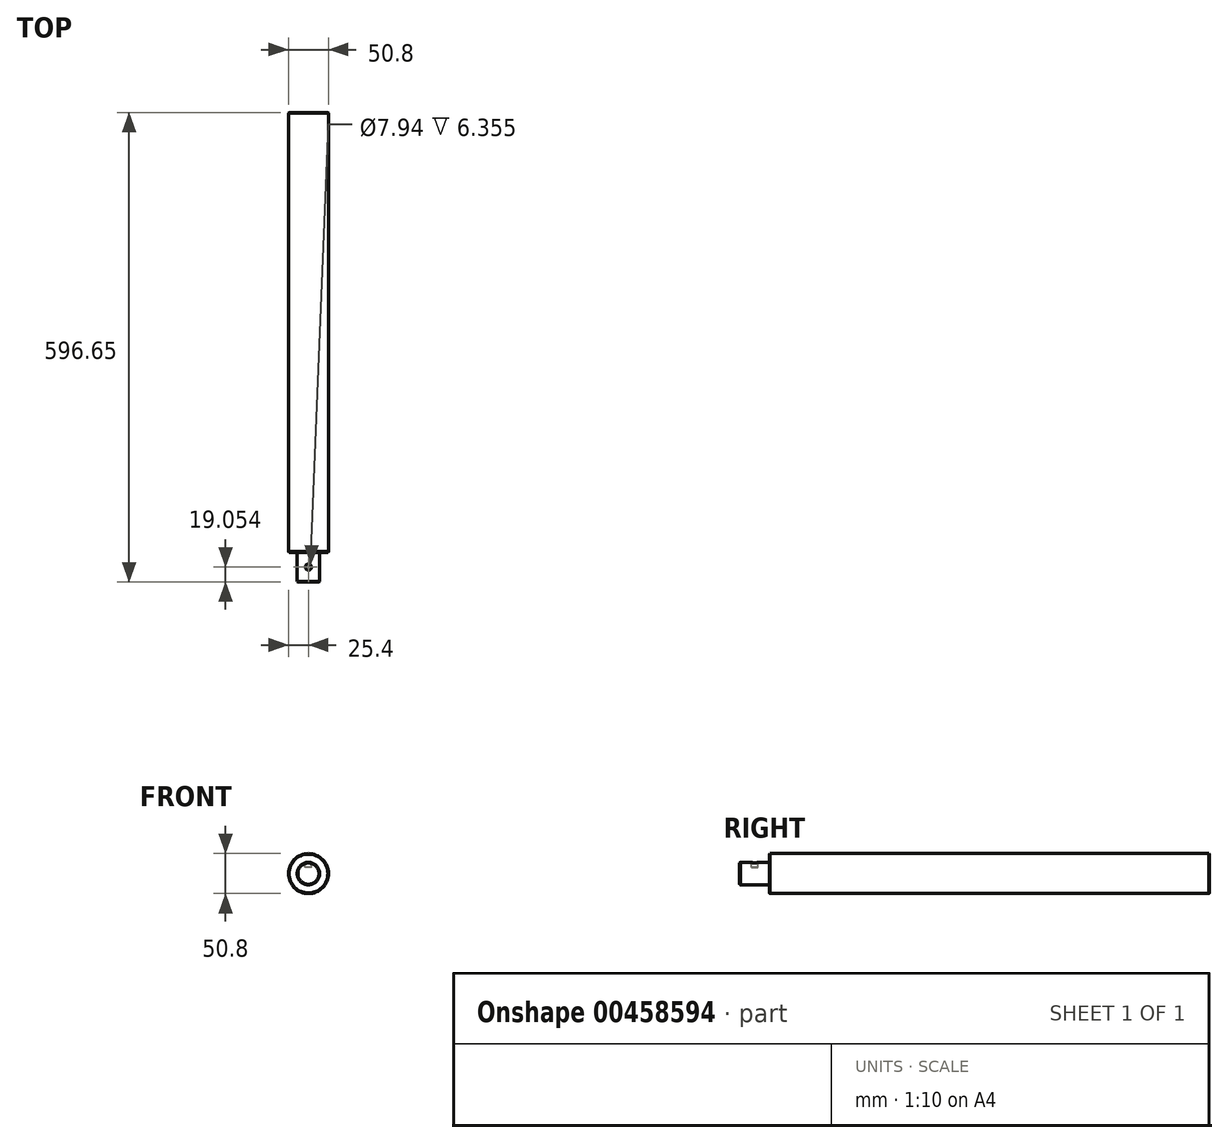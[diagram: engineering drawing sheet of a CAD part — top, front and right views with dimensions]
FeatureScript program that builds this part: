
annotation { "Feature Type Name" : "Feature", "Feature Type Description" : "" }
export const myFeature = defineFeature(function(context is Context, id is Id, definition is map)
    precondition{}
    {
        {
            var Q0;
            Q0=qCreatedBy(makeId("Front.planeOp"),FACE);
            var sketch = newSketch(context, id + "F0", { "sketchPlane" : qUnion([Q0])});
            skCircle(sketch, "E0", {"center": v(0, 0) * mm, "radius": 25.4 * mm});
            skSolve(sketch);
        }
        {
            var Q0;
            Q0 = qSketchRegion(id + "F0", true);
            extrude(context, id + "F1", {"entities" : qUnion([Q0]), "depth" : 558.8 * mm});
        }
        {
            var Q0;
            Q0=makeQuery(id+"F1.opExtrude","CAP_FACE",FACE,{"disambiguationData":[OSD([sQuery(id+"F0.wireOp",EDGE,"E0")])],"isStart":false});
            var sketch = newSketch(context, id + "F2", { "sketchPlane" : qUnion([Q0])});
            skCircle(sketch, "E1", {"center": v(0, 0) * mm, "radius": 14.22 * mm});
            skSolve(sketch);
        }
        {
            var Q0;
            Q0 = qSketchRegion(id + "F2", true);
            extrude(context, id + "F3", {"entities" : qUnion([Q0]), "operationType" : NewBodyOperationType.ADD, "depth" : 37.85 * mm});
        }
        {
            var Q0;
            Q0=makeQuery(id+"F3.opExtrude","CAP_EDGE",EDGE,{"disambiguationData":[OSD([sQuery(id+"F2.wireOp",EDGE,"E1")])],"isStart":false});
            var Q1;
            Q1=makeQuery(id+"F1.opExtrude","CAP_EDGE",EDGE,{"disambiguationData":[OSD([sQuery(id+"F0.wireOp",EDGE,"E0")])],"isStart":false});
            var Q2;
            Q2=makeQuery(id+"F1.opExtrude","CAP_EDGE",EDGE,{"disambiguationData":[OSD([sQuery(id+"F0.wireOp",EDGE,"E0")])],"isStart":true});
            chamfer(context, id + "F4", {"entities" : qUnion([Q0, Q1, Q2]), "width" : 0.76 * mm, "tangentPropagation" : true});
        }
        {
            var Q0;
            Q0=qCreatedBy(makeId("Top.planeOp"),FACE);
            cPlane(context, id + "F5", {"entities" : qUnion([Q0]), "cplaneType" : CPlaneType.OFFSET, "offset" : 14.22 * mm, "width" : 152.4 * mm, "height" : 152.4 * mm});
        }
        {
            var Q0;
            Q0=qCreatedBy(id+"F5.planeOp",FACE);
            var sketch = newSketch(context, id + "F6", { "sketchPlane" : qUnion([Q0])});
            skCircle(sketch, "E2", {"center": v(0, -577.6) * mm, "radius": 3.97 * mm});
            skSolve(sketch);
        }
        {
            var Q0;
            Q0 = qSketchRegion(id + "F6", true);
            extrude(context, id + "F7", {"entities" : qUnion([Q0]), "operationType" : NewBodyOperationType.REMOVE, "oppositeDirection" : true, "depth" : 6.35 * mm});
        }
    });
